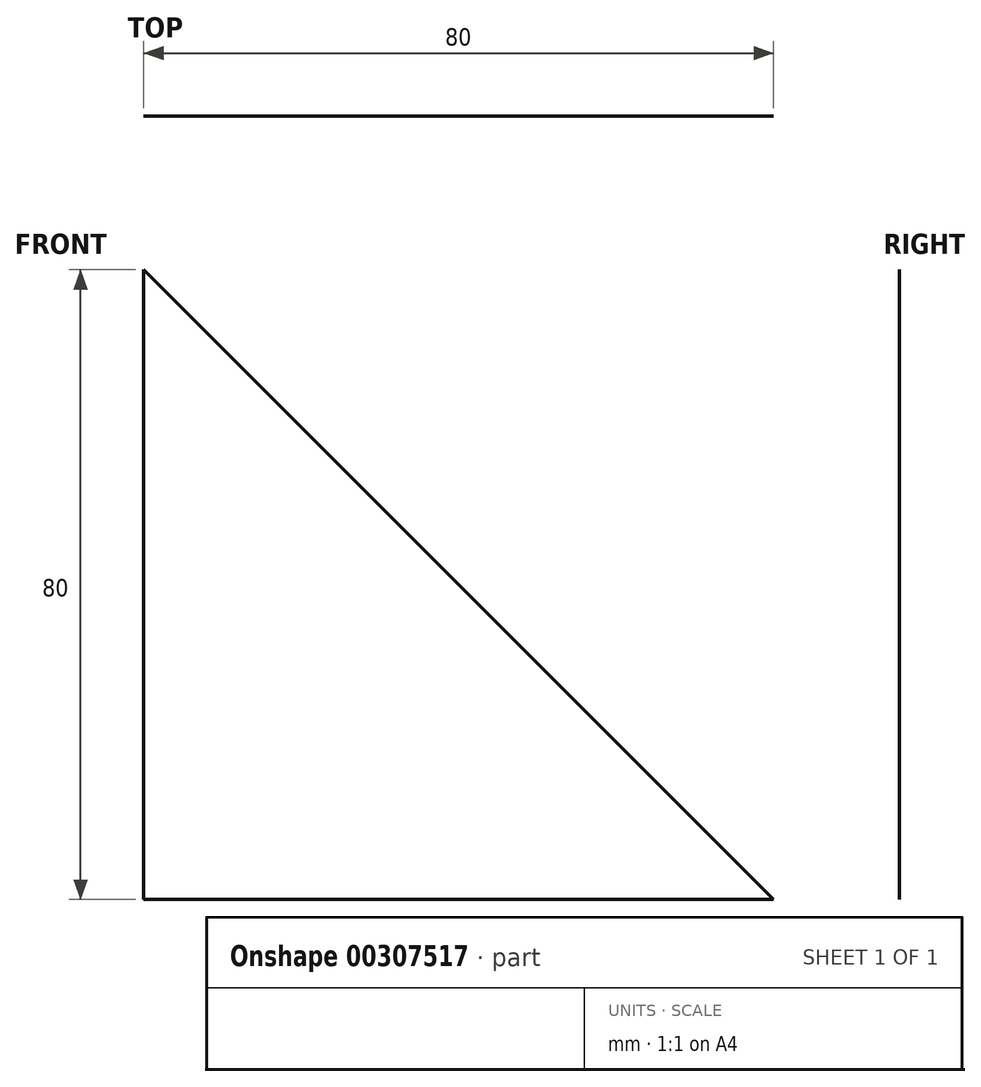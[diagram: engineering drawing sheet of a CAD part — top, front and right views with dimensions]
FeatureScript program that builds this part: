
annotation { "Feature Type Name" : "Feature", "Feature Type Description" : "" }
export const myFeature = defineFeature(function(context is Context, id is Id, definition is map)
    precondition{}
    {
        {
            var Q0;
            Q0=qCreatedBy(makeId("Front.planeOp"),FACE);
            var sketch = newSketch(context, id + "F0", { "sketchPlane" : qUnion([Q0])});
            skLineSegment(sketch, "E0", {"start": v(0, 0) * mm, "end": v(0, 80) * mm});
            skLineSegment(sketch, "E1", {"start": v(0, 80) * mm, "end": v(80, 0) * mm});
            skLineSegment(sketch, "E2", {"start": v(80, 0) * mm, "end": v(0, 0) * mm});
            skSolve(sketch);
        }
        {
            var Q0;
            Q0 = qSketchRegion(id + "F0", true);
            extrude(context, id + "F1", {"entities" : qUnion([Q0]), "endBound" : BoundingType.SYMMETRIC, "depth" : 1 / 203.2 * mm});
        }
    });
